# Revit family: ATAG_CV_ketel_Q25_en_Q38_solo
name_source: partatom
category: Mechanical Equipment
revit_build: Autodesk Revit 2014 (Build: 20130308_1515(x64)
units: mm (PartAtom-declared; Revit-internal decimal feet)

## types (1)
- ATAG_CV_ketel_Q25_en_Q38_solo
    BCB_I BaseKeynote = 56.10.10.13.01
    BCB_I Belasting op bovenwaarde CV = 0 W
    BCB_I Belasting op onderwaarde CV = 0 W
    BCB_I Beschermingsgraad vlgs. EN 60529 = IPX0D
    BCB_I Beschikbare opvoerhoogte pomp CV = 0.00 Pa
    BCB_I Gaskeur HR Top = HR Top
    BCB_I Gaskeur SV_gaskeurlabel schone verbranding = SV
    BCB_I Gewicht (leeg) = 0
    BCB_V Aansluitdiameter CVr = 28 mm
    BCB_V Aansluitdiameter CVv = 28 mm
    BCB_V Aansluitdiameter condensafvoer = 24 mm
    BCB_V Aansluitdiameter gas = 15 mm
    BCB_V Aansluitdiameter luchttoevoer = 80 mm  [stored 0.262467 ft]
    BCB_V Aansluitdiameter rookgasafvoer = 80 mm  [stored 0.262467 ft]
    BCB_V Luchtinlaat_materiaal = BE Kunststof_zwart
    BCB_c1 Debiet = 0 CFM
    BCB_c1 Omschrijving = c1_Rookgasafvoer
    BCB_c1 Straal = 40 mm  [stored 0.131234 ft]
    BCB_c2 Omschrijving = c2_Elektrische voeding
    BCB_c3 Debiet = 0.0000 L/s
    BCB_c3 Energie_inhoud gas = 0 kWh
    BCB_c3 Omschrijving = c3_Gasaansluiting
    BCB_c3 Straal = 8 mm  [stored 0.0262467 ft]
    BCB_c3 Vermogen = 0 kW
    BCB_c4 Omschrijving = c4_CV-toevoer
    BCB_c4 Straal = 14 mm  [stored 0.0459318 ft]
    BCB_c5 Omschrijving = c5_CV-retour
    BCB_c5 Straal = 14 mm  [stored 0.0459318 ft]
    BCB_c6 Omschrijving = c6_Condensafvoer
    BCB_c6 Straal = 12 mm  [stored 0.0393701 ft]
    BCB_c7 Debiet = 0 CFM
    BCB_c7 Omschrijving = c7_Luchttoevoer
    BCB_c7 Straal = 40 mm  [stored 0.131234 ft]
    Default Elevation = 1000 mm  [stored 3.28084 ft]
    GTIN-14 = -
    IFC_versie = 2x3
    IfcExportAs = IfcGasTerminalType
    IfcExportType = gasappliance
    Manufacturer = ATAG
    Model = Q-serie
    NL_E Aantal polen = 1
    NL_E Arbeidsfactor = 1
    NL_E Belastingsklasse = Other
    NL_E Belastingssubklasse motor = No
    NL_E Schijnbaar vermogen = 0 VA
    NL_E Spanning = 230 V
    NL_E Vermogen = 0 W
    NL_G Breedte = 500 mm  [stored 1.64042 ft]
    NL_G Diepte = 385 mm  [stored 1.26312 ft]
    NL_G Hoogte = 680 mm  [stored 2.23097 ft]
    NL_I Bestelcode = -
    NL_M Debiet = 0 CFM
    NL_P FBW = 0.5
    Type Comments = wandketel
    ZZ_Z Aansluiting CV_geen accessoire = NL_M Accessoires aansluitingen CV : Geen
    ZZ_Z Aansluiting CVr_X coördinaat = 35 mm  [stored 0.114829 ft]
    ZZ_Z Aansluiting CVr_Y coördinaat = -143 mm
    ZZ_Z Aansluiting CVr_type accessoire = NL_M Accessoires aansluitingen CV : Kraan
    ZZ_Z Aansluiting CVv_X coördinaat = -65 mm  [stored -0.213255 ft]
    ZZ_Z Aansluiting CVv_Y coördinaat = -143 mm
    ZZ_Z Aansluiting CVv_type accessoire = NL_M Accessoires aansluitingen CV : Kraan
    ZZ_Z Aansluiting gas_X coördinaat = -185 mm  [stored -0.606955 ft]
    ZZ_Z Aansluiting gas_Y coördinaat = -153 mm
    ZZ_Z Aansluiting gas_geen accessoire = NL_M Accessoires aansluitingen gas : Geen
    ZZ_Z Aansluiting gas_type accessoire = NL_M Accessoires aansluitingen gas : Kraan
    ZZ_Z Aansluiting luchttoevoer_X coördinaat = -85 mm  [stored -0.278871 ft]
    ZZ_Z Aansluiting luchttoevoer_Y coördinaat = -43 mm
    ZZ_Z Aansluiting rookgas_X coördinaat = -85 mm  [stored -0.278871 ft]
    ZZ_Z Aansluiting rookgas_Y coördinaat = 78 mm
    ZZ_Z Aansluiting rookgas_linkerzijde = 335 mm
    ZZ_Z Binnendiameter rookgasafvoer = 60 mm  [stored 0.19685 ft]
    ZZ_Z Condensafvoer_X coördinaat = 120 mm  [stored 0.393701 ft]
    ZZ_Z Condensafvoer_Y coördinaat = -168 mm
    ZZ_Z Condensafvoer_accessoire = NL_M Accessoires aansluitingen CV : Geen
    ZZ_Z Expansievat_breedte = 0 mm  [stored 0 ft]
    ZZ_Z Expansievat_breedte2 = 1 mm  [stored 0.00328084 ft]
    ZZ_Z Expansievat_diepte = 0 mm  [stored 0 ft]
    ZZ_Z Expansievat_diepte2 = 1 mm  [stored 0.00328084 ft]
    ZZ_Z Expansievat_hoogte = 0 mm  [stored 0 ft]
    ZZ_Z Expansievat_hoogte2 = 1 mm  [stored 0.00328084 ft]
    ZZ_Z Expansievatmodule = No
    ZZ_Z Halve breedte negatief = -250 mm  [stored -0.82021 ft]
    ZZ_Z Ketel_afstand = 0 mm  [stored 0 ft]
    fabrikant_artikelcode = -
    fabrikant_bibliotheek_versie = v1.0
    fabrikant_jaartal = 2014
    fabrikant_revisie = -
    materiaal = <By Category>
    revit_versie = 2014

note: [stored X ft] marks values corroborated as IEEE doubles in the binary element streams (Revit-internal decimal feet)

## geometry (parser evidence)
native form markers: Blend x2, Sweep x50
no freeform markers — native parametric forms only
